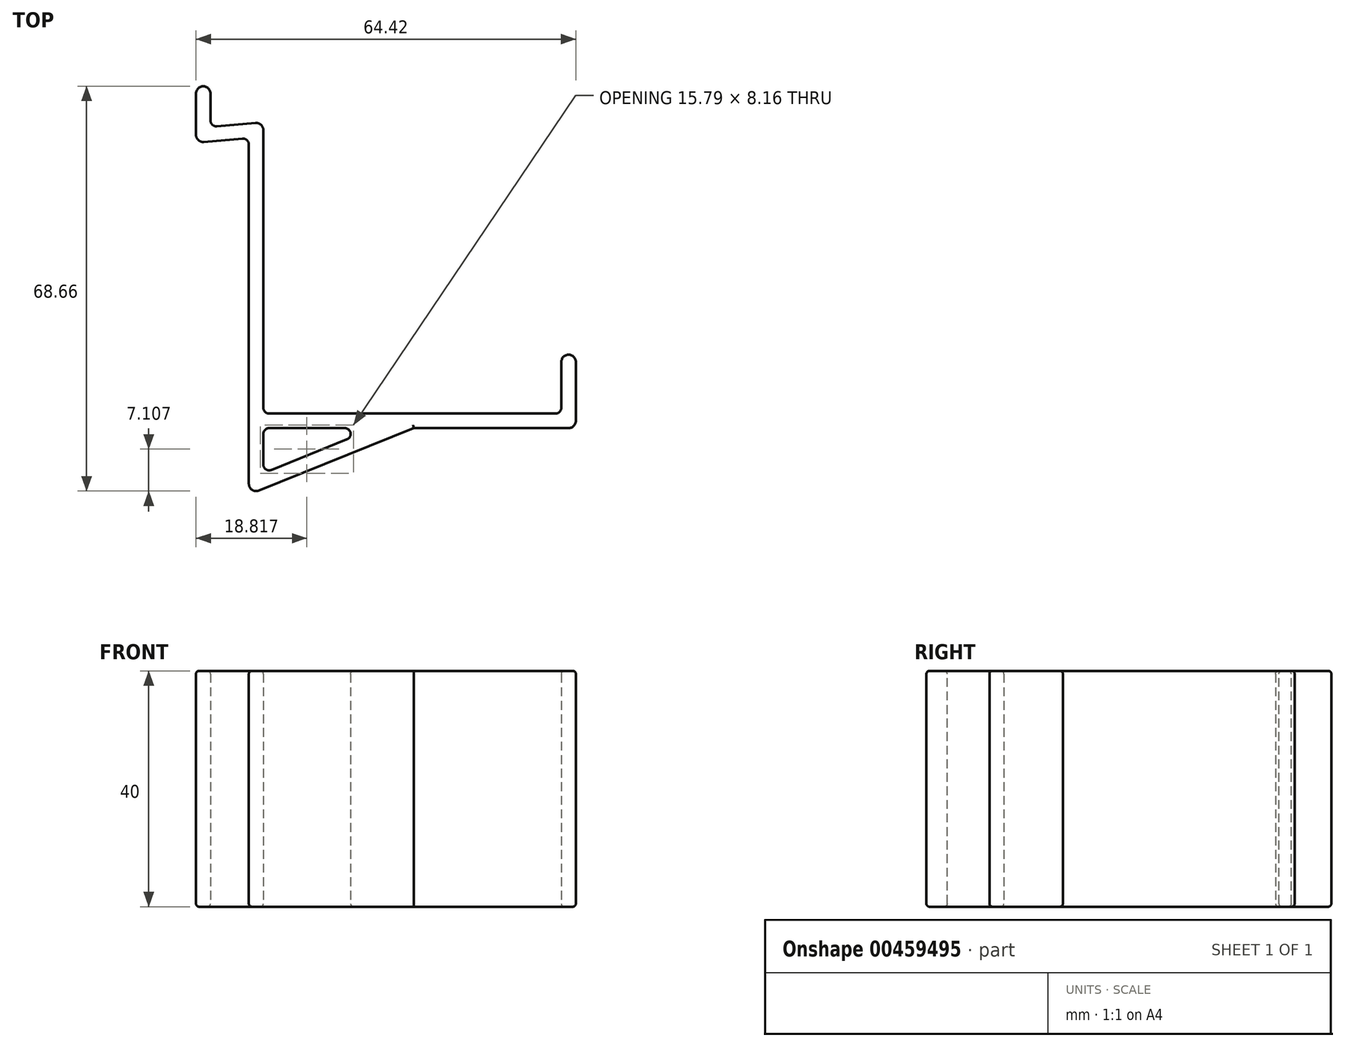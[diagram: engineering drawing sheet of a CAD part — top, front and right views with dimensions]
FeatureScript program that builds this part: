
annotation { "Feature Type Name" : "Feature", "Feature Type Description" : "" }
export const myFeature = defineFeature(function(context is Context, id is Id, definition is map)
    precondition{}
    {
        {
            var Q0;
            Q0=qCreatedBy(makeId("Top.planeOp"),FACE);
            var sketch = newSketch(context, id + "F0", { "sketchPlane" : qUnion([Q0])});
            skLineSegment(sketch, "E0", {"start": v(-18.76, 34.2) * mm, "end": v(-18.76, 27.2) * mm});
            skLineSegment(sketch, "E1", {"start": v(-18.76, 27.2) * mm, "end": v(-9.8, 27.98) * mm});
            skLineSegment(sketch, "E2", {"start": v(-9.8, 27.98) * mm, "end": v(-9.8, -32.02) * mm});
            skLineSegment(sketch, "E3", {"start": v(-9.8, -21.33) * mm, "end": v(43.2, -21.33) * mm});
            skLineSegment(sketch, "E4", {"start": v(43.2, -21.33) * mm, "end": v(43.2, -11.33) * mm});
            skLineSegment(sketch, "E5", {"start": v(-9.8, -32.02) * mm, "end": v(16.7, -21.33) * mm});
            skArc(sketch, "E6.0.startCap", {"start": v(-19.99, 34.2) * mm, "mid": v(-18.76, 35.42) * mm, "end": v(-17.54, 34.2) * mm});
            skArc(sketch, "E6.0.endCap", {"start": v(-17.54, 27.2) * mm, "mid": v(-18.76, 25.97) * mm, "end": v(-19.99, 27.2) * mm});
            skLineSegment(sketch, "E6.0.left", {"start": v(-17.54, 34.2) * mm, "end": v(-17.54, 27.2) * mm});
            skLineSegment(sketch, "E6.0.right", {"start": v(-19.99, 34.2) * mm, "end": v(-19.99, 27.2) * mm});
            skArc(sketch, "E6.1.startCap", {"start": v(-18.65, 25.98) * mm, "mid": v(-19.98, 27.1) * mm, "end": v(-18.87, 28.42) * mm});
            skArc(sketch, "E6.1.endCap", {"start": v(-9.9, 29.2) * mm, "mid": v(-8.57, 28.09) * mm, "end": v(-9.69, 26.76) * mm});
            skLineSegment(sketch, "E6.1.left", {"start": v(-18.87, 28.42) * mm, "end": v(-9.9, 29.2) * mm});
            skLineSegment(sketch, "E6.1.right", {"start": v(-18.65, 25.98) * mm, "end": v(-9.69, 26.76) * mm});
            skArc(sketch, "E6.2.startCap", {"start": v(-11.02, 27.98) * mm, "mid": v(-9.8, 29.2) * mm, "end": v(-8.57, 27.98) * mm});
            skArc(sketch, "E6.2.endCap", {"start": v(-8.57, -32.02) * mm, "mid": v(-9.8, -33.24) * mm, "end": v(-11.02, -32.02) * mm});
            skLineSegment(sketch, "E6.2.left", {"start": v(-8.57, 27.98) * mm, "end": v(-8.57, -32.02) * mm});
            skLineSegment(sketch, "E6.2.right", {"start": v(-11.02, 27.98) * mm, "end": v(-11.02, -32.02) * mm});
            skArc(sketch, "E6.3.startCap", {"start": v(-9.8, -22.55) * mm, "mid": v(-11.02, -21.33) * mm, "end": v(-9.8, -20.1) * mm});
            skArc(sketch, "E6.3.endCap", {"start": v(43.2, -20.1) * mm, "mid": v(44.43, -21.33) * mm, "end": v(43.2, -22.55) * mm});
            skLineSegment(sketch, "E6.3.left", {"start": v(-9.8, -20.1) * mm, "end": v(43.2, -20.1) * mm});
            skLineSegment(sketch, "E6.3.right", {"start": v(-9.8, -22.55) * mm, "end": v(43.2, -22.55) * mm});
            skArc(sketch, "E6.4.startCap", {"start": v(-9.34, -33.15) * mm, "mid": v(-10.93, -32.48) * mm, "end": v(-10.25, -30.88) * mm});
            skArc(sketch, "E6.4.endCap", {"start": v(16.25, -20.2) * mm, "mid": v(17.84, -20.87) * mm, "end": v(17.16, -22.46) * mm});
            skLineSegment(sketch, "E6.4.left", {"start": v(-10.25, -30.88) * mm, "end": v(16.25, -20.2) * mm});
            skLineSegment(sketch, "E6.4.right", {"start": v(-9.34, -33.15) * mm, "end": v(17.16, -22.46) * mm});
            skArc(sketch, "E6.5.startCap", {"start": v(44.43, -21.33) * mm, "mid": v(43.2, -22.55) * mm, "end": v(41.98, -21.33) * mm});
            skArc(sketch, "E6.5.endCap", {"start": v(41.98, -11.33) * mm, "mid": v(43.2, -10.1) * mm, "end": v(44.43, -11.33) * mm});
            skLineSegment(sketch, "E6.5.left", {"start": v(41.98, -21.33) * mm, "end": v(41.98, -11.33) * mm});
            skLineSegment(sketch, "E6.5.right", {"start": v(44.43, -21.33) * mm, "end": v(44.43, -11.33) * mm});
            skSolve(sketch);
        }
        {
            var Q0;
            Q0 = qSketchRegion(id + "F0", true);
            var Q1;
            {var subQ0=sQuery(id+"F0.wireOp",EDGE,"E6.2.left");var subQ1=sQuery(id+"F0.wireOp",EDGE,"E3");var subQ2=makeQuery(id+"F0.imprint","INTERSECT",VERTEX,{"derivedFrom":[subQ1,subQ0]});Q1=makeQuery(id+"F0.imprint","IMPRINT",FACE,{"disambiguationData":[TD([[makeQuery(id+"F0.imprint","IMPRINT",EDGE,{"disambiguationData":[TD([[subQ2,-1.0]])],"derivedFrom":subQ1}),-1.0]])]});}
            var Q2;
            {var subQ0=sQuery(id+"F0.wireOp",EDGE,"E5");var subQ1=sQuery(id+"F0.wireOp",EDGE,"E3");var subQ2=makeQuery(id+"F0.imprint","INTERSECT",VERTEX,{"derivedFrom":[subQ1,subQ0]});Q2=makeQuery(id+"F0.imprint","IMPRINT",FACE,{"disambiguationData":[TD([[makeQuery(id+"F0.imprint","IMPRINT",EDGE,{"disambiguationData":[TD([[subQ2,1.0]])],"derivedFrom":subQ1}),-1.0]])]});}
            var Q3;
            {var subQ0=sQuery(id+"F0.wireOp",EDGE,"E6.2.left");var subQ1=sQuery(id+"F0.wireOp",EDGE,"E5");var subQ2=makeQuery(id+"F0.imprint","INTERSECT",VERTEX,{"derivedFrom":[subQ1,subQ0]});Q3=makeQuery(id+"F0.imprint","IMPRINT",FACE,{"disambiguationData":[TD([[makeQuery(id+"F0.imprint","IMPRINT",EDGE,{"disambiguationData":[TD([[subQ2,-1.0]])],"derivedFrom":subQ1}),1.0]])]});}
            var Q4;
            {var subQ0=sQuery(id+"F0.wireOp",EDGE,"E6.3.right");var subQ5=sQuery(id+"F0.wireOp",EDGE,"E6.2.left");var subQ6=makeQuery(id+"F0.imprint","INTERSECT",VERTEX,{"derivedFrom":[subQ5,subQ0]});Q4=makeQuery(id+"F0.imprint","IMPRINT",FACE,{"disambiguationData":[TD([[makeQuery(id+"F0.imprint","IMPRINT",EDGE,{"disambiguationData":[TD([[subQ6,-1.0]])],"derivedFrom":subQ5}),-1.0]])]});}
            var Q5;
            {var subQ0=sQuery(id+"F0.wireOp",EDGE,"E3");var subQ1=sQuery(id+"F0.wireOp",EDGE,"E2");var subQ2=makeQuery(id+"F0.imprint","INTERSECT",VERTEX,{"derivedFrom":[subQ1,subQ0]});Q5=makeQuery(id+"F0.imprint","IMPRINT",FACE,{"disambiguationData":[TD([[makeQuery(id+"F0.imprint","IMPRINT",EDGE,{"disambiguationData":[TD([[subQ2,-1.0]])],"derivedFrom":subQ0}),-1.0]])]});}
            var Q6;
            {var subQ0=sQuery(id+"F0.wireOp",EDGE,"E5");var subQ1=sQuery(id+"F0.wireOp",EDGE,"E2");var subQ2=makeQuery(id+"F0.imprint","INTERSECT",VERTEX,{"derivedFrom":[subQ1,subQ0]});Q6=makeQuery(id+"F0.imprint","IMPRINT",FACE,{"disambiguationData":[TD([[makeQuery(id+"F0.imprint","IMPRINT",EDGE,{"disambiguationData":[TD([[subQ2,1.0]])],"derivedFrom":subQ1}),1.0]])]});}
            extrude(context, id + "F1", {"entities" : qUnion([Q0, Q1, Q2, Q3, Q4, Q5, Q6]), "depth" : 40 * mm, "offsetDistance" : 25 * mm});
        }
        {
            var Q0;
            Q0=makeQuery(id+"F1.opExtrude","SWEPT_EDGE",EDGE,{"disambiguationData":[OSD([sQuery(id+"F0.wireOp",EDGE,"E6.2.left"),sQuery(id+"F0.wireOp",EDGE,"E6.3.right")])]});
            var Q1;
            Q1=makeQuery(id+"F1.opExtrude","SWEPT_EDGE",EDGE,{"disambiguationData":[OSD([sQuery(id+"F0.wireOp",EDGE,"E6.3.right"),sQuery(id+"F0.wireOp",EDGE,"E6.4.left")])]});
            var Q2;
            Q2=makeQuery(id+"F1.opExtrude","SWEPT_EDGE",EDGE,{"disambiguationData":[OSD([sQuery(id+"F0.wireOp",EDGE,"E6.2.left"),sQuery(id+"F0.wireOp",EDGE,"E6.4.left")])]});
            var Q3;
            Q3=makeQuery(id+"F1.opExtrude","SWEPT_EDGE",EDGE,{"disambiguationData":[OSD([sQuery(id+"F0.wireOp",EDGE,"E6.2.left"),sQuery(id+"F0.wireOp",EDGE,"E6.3.left")])]});
            var Q4;
            Q4=makeQuery(id+"F1.opExtrude","SWEPT_EDGE",EDGE,{"disambiguationData":[OSD([sQuery(id+"F0.wireOp",EDGE,"E6.3.left"),sQuery(id+"F0.wireOp",EDGE,"E6.5.left")])]});
            var Q5;
            Q5=makeQuery(id+"F1.opExtrude","SWEPT_EDGE",EDGE,{"disambiguationData":[OSD([sQuery(id+"F0.wireOp",EDGE,"E6.0.left"),sQuery(id+"F0.wireOp",EDGE,"E6.1.left")])]});
            var Q6;
            Q6=makeQuery(id+"F1.opExtrude","SWEPT_EDGE",EDGE,{"disambiguationData":[OSD([sQuery(id+"F0.wireOp",EDGE,"E6.1.right"),sQuery(id+"F0.wireOp",EDGE,"E6.2.right")])]});
            fillet(context, id + "F2", {"entities" : qUnion([Q0, Q1, Q2, Q3, Q4, Q5, Q6]), "radius" : 1 * mm, "tangentPropagation" : true, "allowEdgeOverflow" : false});
        }
        {
            var Q0;
            Q0=makeQuery(id+"F1.opExtrude","CAP_FACE",FACE,{"disambiguationData":[OSD([sQuery(id+"F0.wireOp",EDGE,"E6.0.startCap"),sQuery(id+"F0.wireOp",EDGE,"E6.0.left"),sQuery(id+"F0.wireOp",EDGE,"E6.0.right"),sQuery(id+"F0.wireOp",EDGE,"E6.1.startCap"),sQuery(id+"F0.wireOp",EDGE,"E6.1.left"),sQuery(id+"F0.wireOp",EDGE,"E6.1.right"),sQuery(id+"F0.wireOp",EDGE,"E6.2.startCap"),sQuery(id+"F0.wireOp",EDGE,"E6.2.left"),sQuery(id+"F0.wireOp",EDGE,"E6.2.right"),sQuery(id+"F0.wireOp",EDGE,"E6.3.left"),sQuery(id+"F0.wireOp",EDGE,"E6.3.right"),sQuery(id+"F0.wireOp",EDGE,"E6.4.startCap"),sQuery(id+"F0.wireOp",EDGE,"E6.4.left"),sQuery(id+"F0.wireOp",EDGE,"E6.4.right"),sQuery(id+"F0.wireOp",EDGE,"E6.5.startCap"),sQuery(id+"F0.wireOp",EDGE,"E6.5.endCap"),sQuery(id+"F0.wireOp",EDGE,"E6.5.left"),sQuery(id+"F0.wireOp",EDGE,"E6.5.right")])],"isStart":false});
            var Q1;
            Q1=makeQuery(id+"F1.opExtrude","CAP_FACE",FACE,{"disambiguationData":[OSD([sQuery(id+"F0.wireOp",EDGE,"E6.0.startCap"),sQuery(id+"F0.wireOp",EDGE,"E6.0.left"),sQuery(id+"F0.wireOp",EDGE,"E6.0.right"),sQuery(id+"F0.wireOp",EDGE,"E6.1.startCap"),sQuery(id+"F0.wireOp",EDGE,"E6.1.left"),sQuery(id+"F0.wireOp",EDGE,"E6.1.right"),sQuery(id+"F0.wireOp",EDGE,"E6.2.startCap"),sQuery(id+"F0.wireOp",EDGE,"E6.2.left"),sQuery(id+"F0.wireOp",EDGE,"E6.2.right"),sQuery(id+"F0.wireOp",EDGE,"E6.3.left"),sQuery(id+"F0.wireOp",EDGE,"E6.3.right"),sQuery(id+"F0.wireOp",EDGE,"E6.4.startCap"),sQuery(id+"F0.wireOp",EDGE,"E6.4.left"),sQuery(id+"F0.wireOp",EDGE,"E6.4.right"),sQuery(id+"F0.wireOp",EDGE,"E6.5.startCap"),sQuery(id+"F0.wireOp",EDGE,"E6.5.endCap"),sQuery(id+"F0.wireOp",EDGE,"E6.5.left"),sQuery(id+"F0.wireOp",EDGE,"E6.5.right")])],"isStart":true});
            fillet(context, id + "F3", {"entities" : qUnion([Q0, Q1]), "radius" : 0.5 * mm, "tangentPropagation" : true, "allowEdgeOverflow" : false});
        }
    });
